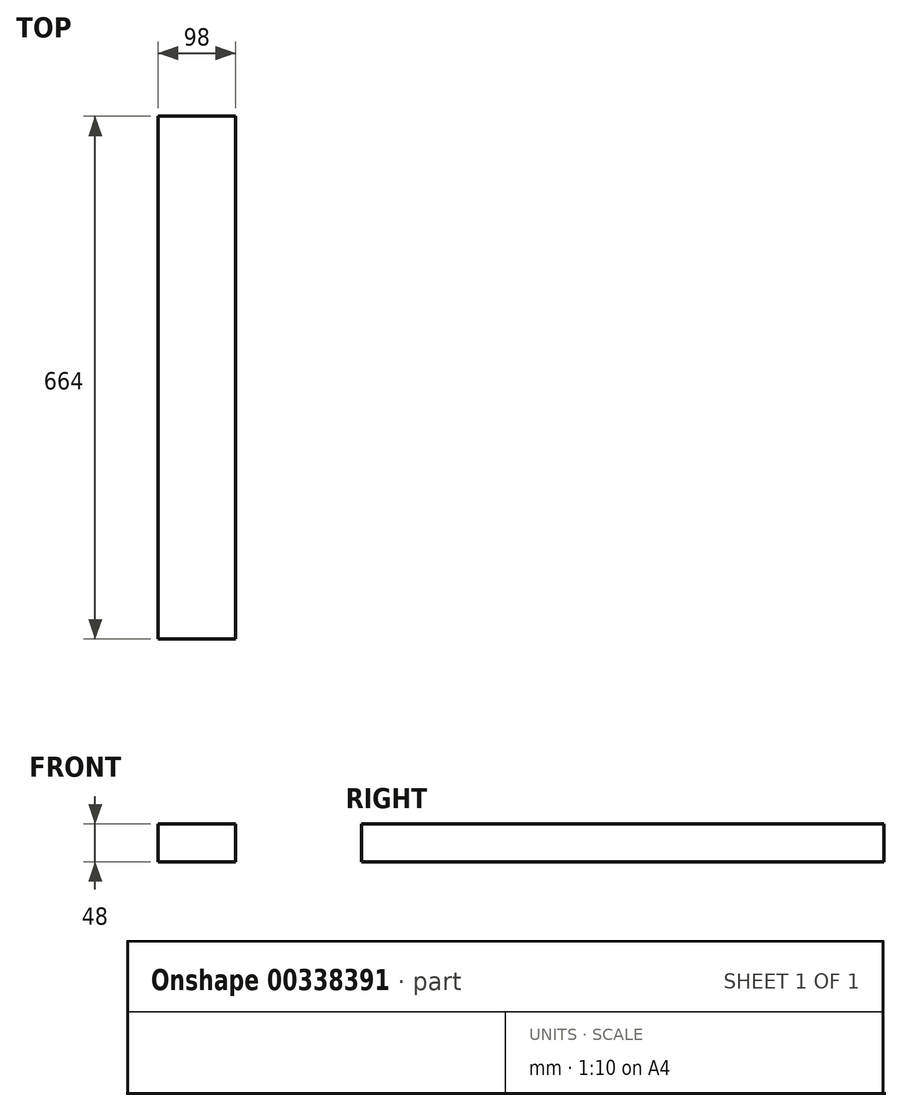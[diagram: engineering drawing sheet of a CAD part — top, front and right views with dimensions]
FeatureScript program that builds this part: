
annotation { "Feature Type Name" : "Feature", "Feature Type Description" : "" }
export const myFeature = defineFeature(function(context is Context, id is Id, definition is map)
    precondition{}
    {
        {
            var Q0;
            Q0=qCreatedBy(makeId("Front.planeOp"),FACE);
            var sketch = newSketch(context, id + "F0", { "sketchPlane" : qUnion([Q0])});
            skLineSegment(sketch, "E0.bottom", {"start": v(-49, -24) * mm, "end": v(49, -24) * mm});
            skLineSegment(sketch, "E0.top", {"start": v(-49, 24) * mm, "end": v(49, 24) * mm});
            skLineSegment(sketch, "E0.left", {"start": v(-49, -24) * mm, "end": v(-49, 24) * mm});
            skLineSegment(sketch, "E0.right", {"start": v(49, -24) * mm, "end": v(49, 24) * mm});
            skPoint(sketch, "E0.middle", {"position": v(0, 0) * mm});
            skSolve(sketch);
        }
        {
            var Q0;
            Q0=makeQuery(id+"F0.imprint","IMPRINT",FACE,{"disambiguationData":[TD([[makeQuery(id+"F0.imprint","IMPRINT",EDGE,{"derivedFrom":sQuery(id+"F0.wireOp",EDGE,"E0.bottom")}),1.0]])]});
            extrude(context, id + "F1", {"entities" : qUnion([Q0]), "offsetDistance" : 25 * mm, "depth" : 664 * mm});
        }
    });
